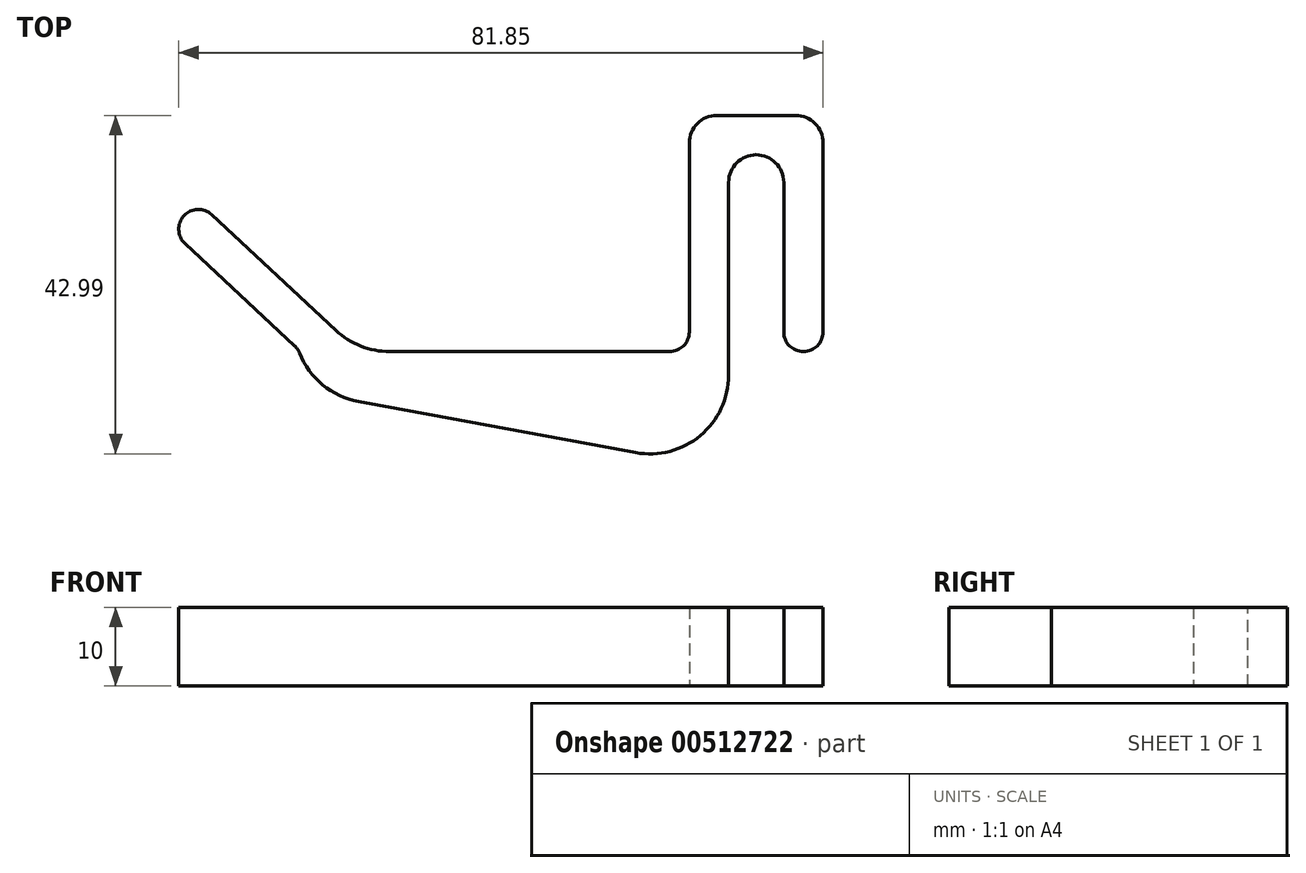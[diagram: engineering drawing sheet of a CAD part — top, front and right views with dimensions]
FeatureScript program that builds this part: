
annotation { "Feature Type Name" : "Feature", "Feature Type Description" : "" }
export const myFeature = defineFeature(function(context is Context, id is Id, definition is map)
    precondition{}
    {
        {
            var Q0;
            Q0=qCreatedBy(makeId("Top.planeOp"),FACE);
            var sketch = newSketch(context, id + "F0", { "sketchPlane" : qUnion([Q0])});
            skLineSegment(sketch, "E0", {"start": v(5, 0) * mm, "end": v(5, 25) * mm});
            skLineSegment(sketch, "E1", {"start": v(5, 25) * mm, "end": v(12, 25) * mm});
            skLineSegment(sketch, "E2", {"start": v(12, 25) * mm, "end": v(12, 0) * mm});
            skLineSegment(sketch, "E3", {"start": v(12, 0) * mm, "end": v(17, 0) * mm});
            skLineSegment(sketch, "E4", {"start": v(17, 0) * mm, "end": v(17, 30) * mm});
            skLineSegment(sketch, "E5", {"start": v(17, 30) * mm, "end": v(0, 30) * mm});
            skLineSegment(sketch, "E6", {"start": v(0, 30) * mm, "end": v(0, 0) * mm});
            skLineSegment(sketch, "E7", {"start": v(5, -15) * mm, "end": v(-49.33, -5) * mm});
            skLineSegment(sketch, "E8", {"start": v(-49.33, -5) * mm, "end": v(-49.33, 0) * mm});
            skLineSegment(sketch, "E9", {"start": v(-49.33, 0) * mm, "end": v(0, 0) * mm});
            skLineSegment(sketch, "E10", {"start": v(5, -15) * mm, "end": v(5, 0) * mm});
            skLineSegment(sketch, "E11", {"start": v(-42, 0) * mm, "end": v(-62.48, 19.1) * mm});
            skLineSegment(sketch, "E12", {"start": v(-62.48, 19.1) * mm, "end": v(-65.89, 15.44) * mm});
            skLineSegment(sketch, "E13", {"start": v(-65.89, 15.44) * mm, "end": v(-49.33, 0) * mm});
            skSolve(sketch);
        }
        {
            var Q0;
            Q0 = qSketchRegion(id + "F0", true);
            extrude(context, id + "F1", {"entities" : qUnion([Q0]), "depth" : 10 * mm, "offsetDistance" : 25 * mm});
        }
        {
            var Q0;
            Q0=makeQuery(id+"F1.opExtrude","SWEPT_EDGE",EDGE,{"disambiguationData":[OSD([sQuery(id+"F0.wireOp",EDGE,"E0"),sQuery(id+"F0.wireOp",EDGE,"E1")])]});
            var Q1;
            Q1=makeQuery(id+"F1.opExtrude","SWEPT_EDGE",EDGE,{"disambiguationData":[OSD([sQuery(id+"F0.wireOp",EDGE,"E1"),sQuery(id+"F0.wireOp",EDGE,"E2")])]});
            var Q2;
            Q2=makeQuery(id+"F1.opExtrude","SWEPT_EDGE",EDGE,{"disambiguationData":[OSD([sQuery(id+"F0.wireOp",EDGE,"E5"),sQuery(id+"F0.wireOp",EDGE,"E6")])]});
            var Q3;
            Q3=makeQuery(id+"F1.opExtrude","SWEPT_EDGE",EDGE,{"disambiguationData":[OSD([sQuery(id+"F0.wireOp",EDGE,"E4"),sQuery(id+"F0.wireOp",EDGE,"E5")])]});
            fillet(context, id + "F2", {"entities" : qUnion([Q0, Q1, Q2, Q3]), "radius" : (7 / 2) * mm, "tangentPropagation" : true, "allowEdgeOverflow" : false});
        }
        {
            var Q0;
            Q0=makeQuery(id+"F1.opExtrude","SWEPT_EDGE",EDGE,{"disambiguationData":[OSD([sQuery(id+"F0.wireOp",EDGE,"E6"),sQuery(id+"F0.wireOp",EDGE,"E9")])]});
            var Q1;
            Q1=makeQuery(id+"F1.opExtrude","SWEPT_EDGE",EDGE,{"disambiguationData":[OSD([sQuery(id+"F0.wireOp",EDGE,"E3"),sQuery(id+"F0.wireOp",EDGE,"E4")])]});
            var Q2;
            Q2=makeQuery(id+"F1.opExtrude","SWEPT_EDGE",EDGE,{"disambiguationData":[OSD([sQuery(id+"F0.wireOp",EDGE,"E2"),sQuery(id+"F0.wireOp",EDGE,"E3")])]});
            var Q3;
            Q3=makeQuery(id+"F1.opExtrude","SWEPT_EDGE",EDGE,{"disambiguationData":[OSD([sQuery(id+"F0.wireOp",EDGE,"E8"),sQuery(id+"F0.wireOp",EDGE,"E9"),sQuery(id+"F0.wireOp",EDGE,"E13")])]});
            var Q4;
            Q4=makeQuery(id+"F1.opExtrude","SWEPT_EDGE",EDGE,{"disambiguationData":[OSD([sQuery(id+"F0.wireOp",EDGE,"E11"),sQuery(id+"F0.wireOp",EDGE,"E12")])]});
            var Q5;
            Q5=makeQuery(id+"F1.opExtrude","SWEPT_EDGE",EDGE,{"disambiguationData":[OSD([sQuery(id+"F0.wireOp",EDGE,"E12"),sQuery(id+"F0.wireOp",EDGE,"E13")])]});
            fillet(context, id + "F3", {"entities" : qUnion([Q0, Q1, Q2, Q3, Q4, Q5]), "radius" : 2.5 * mm, "tangentPropagation" : true, "allowEdgeOverflow" : false});
        }
        {
            var Q0;
            Q0=makeQuery(id+"F1.opExtrude","SWEPT_EDGE",EDGE,{"disambiguationData":[OSD([sQuery(id+"F0.wireOp",EDGE,"E6"),sQuery(id+"F0.wireOp",EDGE,"E9")])]});
            var Q1;
            Q1=makeQuery(id+"F1.opExtrude","SWEPT_EDGE",EDGE,{"disambiguationData":[OSD([sQuery(id+"F0.wireOp",EDGE,"E7"),sQuery(id+"F0.wireOp",EDGE,"E10")])]});
            var Q2;
            Q2=makeQuery(id+"F1.opExtrude","SWEPT_EDGE",EDGE,{"disambiguationData":[OSD([sQuery(id+"F0.wireOp",EDGE,"E7"),sQuery(id+"F0.wireOp",EDGE,"E8")])]});
            var Q3;
            Q3=makeQuery(id+"F1.opExtrude","SWEPT_EDGE",EDGE,{"disambiguationData":[OSD([sQuery(id+"F0.wireOp",EDGE,"E9"),sQuery(id+"F0.wireOp",EDGE,"E11")])]});
            fillet(context, id + "F4", {"entities" : qUnion([Q0, Q1, Q2, Q3]), "radius" : 10 * mm, "tangentPropagation" : true, "allowEdgeOverflow" : false});
        }
    });
